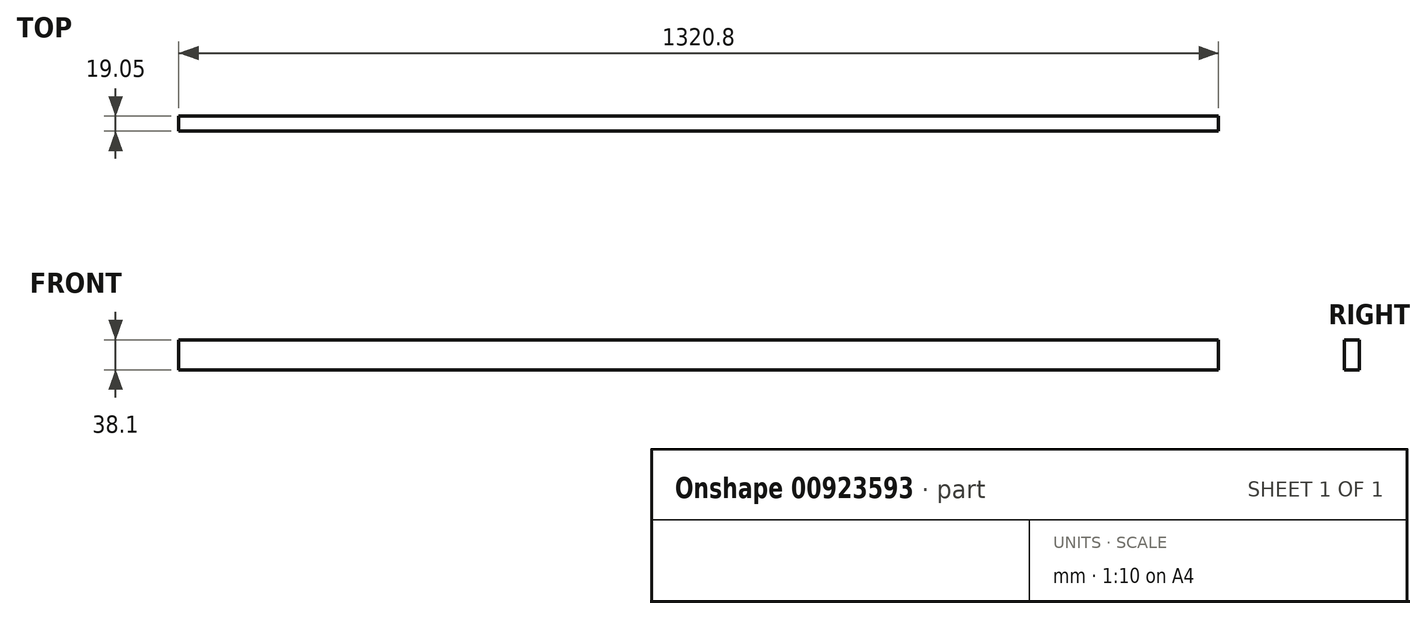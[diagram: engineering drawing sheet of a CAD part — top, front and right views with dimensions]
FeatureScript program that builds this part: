
annotation { "Feature Type Name" : "Feature", "Feature Type Description" : "" }
export const myFeature = defineFeature(function(context is Context, id is Id, definition is map)
    precondition{}
    {
        {
            var Q0;
            Q0=qCreatedBy(makeId("Front.planeOp"),FACE);
            var sketch = newSketch(context, id + "F0", { "sketchPlane" : qUnion([Q0])});
            skLineSegment(sketch, "E0.bottom", {"start": v(0, 0) * mm, "end": v(1320.8, 0) * mm});
            skLineSegment(sketch, "E0.top", {"start": v(0, 38.1) * mm, "end": v(1320.8, 38.1) * mm});
            skLineSegment(sketch, "E0.left", {"start": v(0, 0) * mm, "end": v(0, 38.1) * mm});
            skLineSegment(sketch, "E0.right", {"start": v(1320.8, 0) * mm, "end": v(1320.8, 38.1) * mm});
            skSolve(sketch);
        }
        {
            var Q0;
            Q0 = qSketchRegion(id + "F0", true);
            extrude(context, id + "F1", {"entities" : qUnion([Q0]), "depth" : 19.05 * mm, "offsetDistance" : 25.4 * mm});
        }
    });
